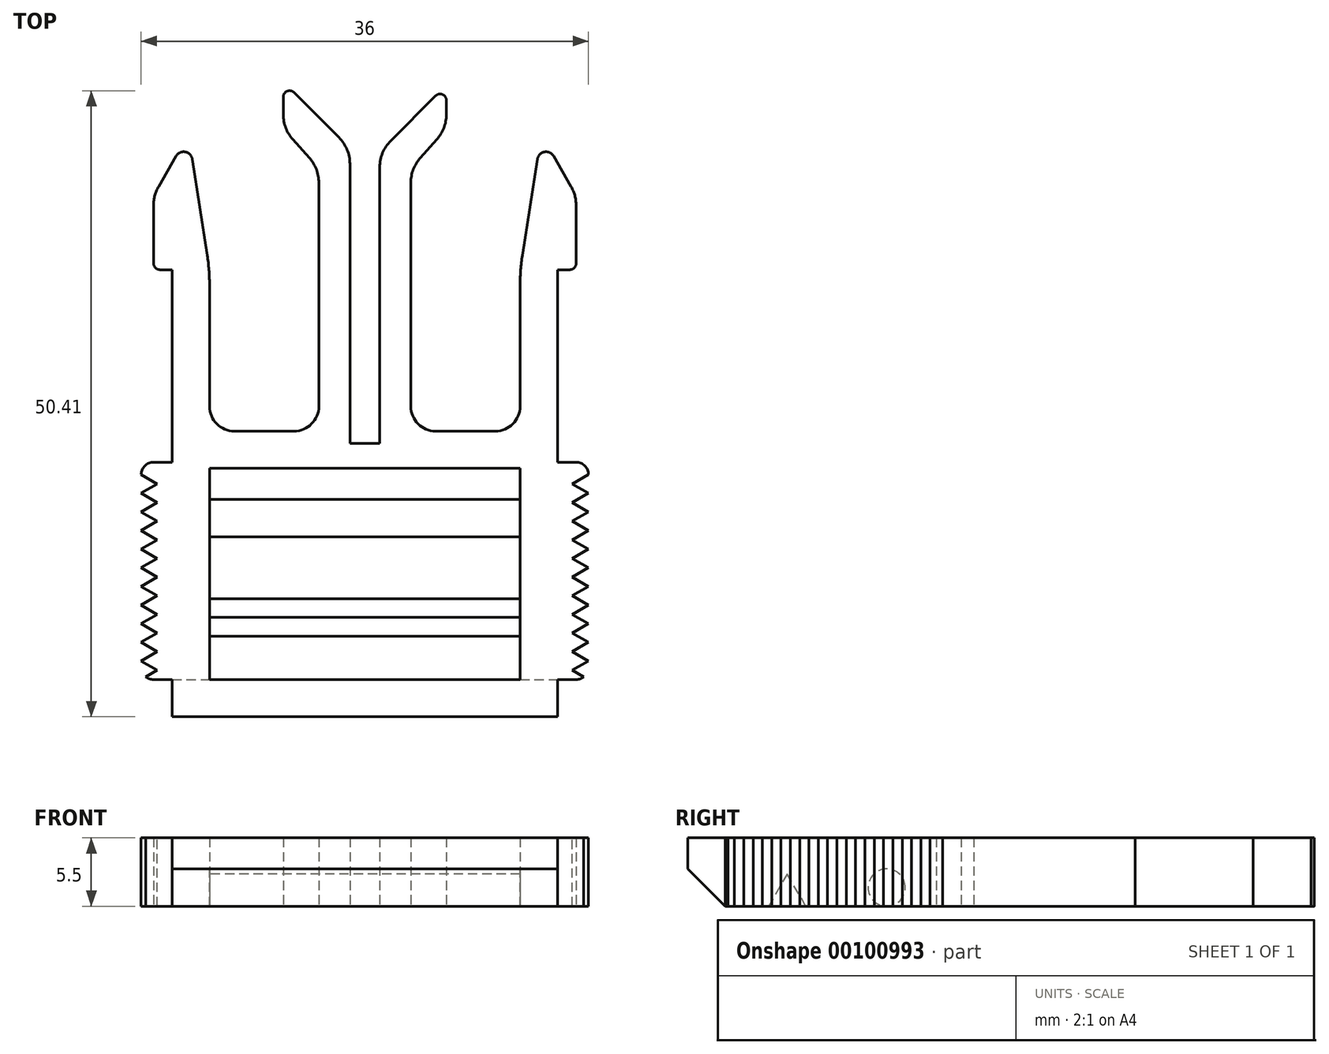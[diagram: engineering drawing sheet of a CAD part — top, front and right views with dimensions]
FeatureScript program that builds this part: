
annotation { "Feature Type Name" : "Feature", "Feature Type Description" : "" }
export const myFeature = defineFeature(function(context is Context, id is Id, definition is map)
    precondition{}
    {
        {
            var Q0;
            Q0=qCreatedBy(makeId("Top.planeOp"),FACE);
            var sketch = newSketch(context, id + "F0", { "sketchPlane" : qUnion([Q0])});
            skLineSegment(sketch, "E0.top", {"start": v(15.5, -24.35) * mm, "end": v(-15.5, -24.35) * mm});
            skPoint(sketch, "E0.middle", {"position": v(0, 0) * mm});
            skLineSegment(sketch, "E1.bottom", {"start": v(12.5, -4.35) * mm, "end": v(-12.5, -4.35) * mm});
            skLineSegment(sketch, "E1.top", {"start": v(12.5, -21.35) * mm, "end": v(-12.5, -21.35) * mm});
            skLineSegment(sketch, "E1.left", {"start": v(12.5, -4.35) * mm, "end": v(12.5, -21.35) * mm});
            skLineSegment(sketch, "E1.right", {"start": v(-12.5, -4.35) * mm, "end": v(-12.5, -21.35) * mm});
            skPoint(sketch, "E1.middle", {"position": v(0, -12.85) * mm});
            skLineSegment(sketch, "E2", {"start": v(15.18, 20.8) * mm, "end": v(16.6, 18.34) * mm});
            skLineSegment(sketch, "E3", {"start": v(17, 16.84) * mm, "end": v(17, 12.15) * mm});
            skLineSegment(sketch, "E4", {"start": v(16.5, 11.65) * mm, "end": v(15.5, 11.65) * mm});
            skLineSegment(sketch, "E5", {"start": v(0, -4.35) * mm, "end": v(0, 27.9) * mm, "construction": true});
            skLineSegment(sketch, "E6", {"start": v(-10.5, -1.35) * mm, "end": v(-5.7, -1.35) * mm});
            skLineSegment(sketch, "E7.trimOffspring", {"start": v(15.5, 11.65) * mm, "end": v(15.5, -24.35) * mm});
            skLineSegment(sketch, "E8", {"start": v(12.5, 10.49) * mm, "end": v(12.5, 0.65) * mm});
            skLineSegment(sketch, "E9.0", {"start": v(-3.7, 0.65) * mm, "end": v(-3.7, 18.65) * mm});
            skLineSegment(sketch, "E10.0", {"start": v(3.7, 0.65) * mm, "end": v(3.7, 18.65) * mm});
            skLineSegment(sketch, "E11", {"start": v(13.89, 20.55) * mm, "end": v(12.68, 12.8) * mm});
            skPoint(sketch, "E12.visualSharp", {"position": v(12.5, 11.65) * mm});
            skArc(sketch, "E12.filletArc", {"start": v(12.68, 12.8) * mm, "mid": v(12.54, 11.64) * mm, "end": v(12.5, 10.49) * mm});
            skLineSegment(sketch, "E13.trimOffspring", {"start": v(5.7, -1.35) * mm, "end": v(10.5, -1.35) * mm});
            skPoint(sketch, "E14.orphan", {"position": v(13.51, 18.14) * mm});
            skPoint(sketch, "E15.orphan", {"position": v(16.29, 18.88) * mm});
            skPoint(sketch, "E16.orphan", {"position": v(15.5, -1.35) * mm});
            skPoint(sketch, "E17.visualSharp", {"position": v(14.2, 22.51) * mm});
            skArc(sketch, "E17.filletArc", {"start": v(15.18, 20.8) * mm, "mid": v(14.45, 21.13) * mm, "end": v(13.89, 20.55) * mm});
            skArc(sketch, "E18.MirrorCS", {"start": v(-15.18, 20.8) * mm, "mid": v(-14.45, 21.13) * mm, "end": v(-13.89, 20.55) * mm});
            skLineSegment(sketch, "E19.MirrorCS", {"start": v(-15.18, 20.8) * mm, "end": v(-16.6, 18.34) * mm});
            skLineSegment(sketch, "E20.MirrorCS", {"start": v(-16.5, 11.65) * mm, "end": v(-15.5, 11.65) * mm});
            skPoint(sketch, "E21.MirrorP", {"position": v(-13.51, 18.14) * mm});
            skPoint(sketch, "E22.MirrorP", {"position": v(-12.5, 11.65) * mm});
            skArc(sketch, "E23.MirrorCS", {"start": v(-12.68, 12.8) * mm, "mid": v(-12.54, 11.64) * mm, "end": v(-12.5, 10.49) * mm});
            skPoint(sketch, "E24.MirrorP", {"position": v(-14.2, 22.51) * mm});
            skPoint(sketch, "E25.MirrorP", {"position": v(-16.29, 18.88) * mm});
            skLineSegment(sketch, "E26.MirrorCS", {"start": v(-17, 16.84) * mm, "end": v(-17, 12.15) * mm});
            skLineSegment(sketch, "E27.MirrorCS", {"start": v(-13.89, 20.55) * mm, "end": v(-12.68, 12.8) * mm});
            skLineSegment(sketch, "E28.MirrorCS", {"start": v(-15.5, 11.65) * mm, "end": v(-15.5, -24.35) * mm});
            skLineSegment(sketch, "E29.MirrorCS", {"start": v(-12.5, 10.49) * mm, "end": v(-12.5, 0.65) * mm});
            skLineSegment(sketch, "E30.0", {"start": v(1.2, -2.35) * mm, "end": v(1.2, 19.9) * mm});
            skLineSegment(sketch, "E31.0", {"start": v(-1.2, -2.35) * mm, "end": v(-1.2, 20.17) * mm});
            skLineSegment(sketch, "E32", {"start": v(5.7, 25.65) * mm, "end": v(2.08, 22.03) * mm});
            skLineSegment(sketch, "E33", {"start": v(-5.7, 25.92) * mm, "end": v(-2.08, 22.29) * mm});
            skPoint(sketch, "E34.visualSharp", {"position": v(17, 17.65) * mm});
            skArc(sketch, "E34.filletArc", {"start": v(17, 16.84) * mm, "mid": v(16.9, 17.62) * mm, "end": v(16.6, 18.34) * mm});
            skPoint(sketch, "E35.visualSharp", {"position": v(-17, 17.65) * mm});
            skArc(sketch, "E35.filletArc", {"start": v(-16.6, 18.34) * mm, "mid": v(-16.9, 17.62) * mm, "end": v(-17, 16.84) * mm});
            skLineSegment(sketch, "E36", {"start": v(-1.2, -2.35) * mm, "end": v(1.2, -2.35) * mm});
            skPoint(sketch, "E37.orphan", {"position": v(1.2, 0.65) * mm});
            skPoint(sketch, "E38.orphan", {"position": v(-1.2, 0.65) * mm});
            skLineSegment(sketch, "E39", {"start": v(4.46, 20.65) * mm, "end": v(5.8, 22.14) * mm});
            skLineSegment(sketch, "E40", {"start": v(6.56, 24.14) * mm, "end": v(6.56, 25.3) * mm});
            skLineSegment(sketch, "E41.MirrorCS", {"start": v(-4.46, 20.65) * mm, "end": v(-5.8, 22.14) * mm});
            skLineSegment(sketch, "E42.MirrorCS", {"start": v(-6.56, 24.14) * mm, "end": v(-6.56, 25.56) * mm});
            skPoint(sketch, "E43.newPointB", {"position": v(6.56, 27.77) * mm});
            skArc(sketch, "E43.filletArc", {"start": v(6.56, 25.3) * mm, "mid": v(6.25, 25.76) * mm, "end": v(5.7, 25.65) * mm});
            skPoint(sketch, "E44.newPointB", {"position": v(-6.56, 27.77) * mm});
            skArc(sketch, "E44.filletArc", {"start": v(-5.7, 25.92) * mm, "mid": v(-6.25, 26.03) * mm, "end": v(-6.56, 25.56) * mm});
            skPoint(sketch, "E45.orphan", {"position": v(3.7, 23.65) * mm});
            skPoint(sketch, "E46.orphan", {"position": v(-3.7, 23.91) * mm});
            skPoint(sketch, "E47.visualSharp", {"position": v(3.7, 19.8) * mm});
            skArc(sketch, "E47.filletArc", {"start": v(4.46, 20.65) * mm, "mid": v(3.9, 19.72) * mm, "end": v(3.7, 18.65) * mm});
            skPoint(sketch, "E48.visualSharp", {"position": v(1.2, 21.15) * mm});
            skArc(sketch, "E48.filletArc", {"start": v(2.08, 22.03) * mm, "mid": v(1.43, 21.05) * mm, "end": v(1.2, 19.9) * mm});
            skPoint(sketch, "E49.visualSharp", {"position": v(-1.2, 21.41) * mm});
            skArc(sketch, "E49.filletArc", {"start": v(-1.2, 20.17) * mm, "mid": v(-1.43, 21.32) * mm, "end": v(-2.08, 22.29) * mm});
            skPoint(sketch, "E50.visualSharp", {"position": v(-3.7, 19.8) * mm});
            skArc(sketch, "E50.filletArc", {"start": v(-3.7, 18.65) * mm, "mid": v(-3.9, 19.72) * mm, "end": v(-4.46, 20.65) * mm});
            skPoint(sketch, "E51.visualSharp", {"position": v(6.56, 23) * mm});
            skArc(sketch, "E51.filletArc", {"start": v(5.8, 22.14) * mm, "mid": v(6.36, 23.07) * mm, "end": v(6.56, 24.14) * mm});
            skPoint(sketch, "E52.visualSharp", {"position": v(-6.56, 23) * mm});
            skArc(sketch, "E52.filletArc", {"start": v(-6.56, 24.14) * mm, "mid": v(-6.36, 23.07) * mm, "end": v(-5.8, 22.14) * mm});
            skPoint(sketch, "E53.visualSharp", {"position": v(12.5, -1.35) * mm});
            skArc(sketch, "E53.filletArc", {"start": v(10.5, -1.35) * mm, "mid": v(11.91, -0.77) * mm, "end": v(12.5, 0.65) * mm});
            skPoint(sketch, "E54.visualSharp", {"position": v(-12.5, -1.35) * mm});
            skArc(sketch, "E54.filletArc", {"start": v(-12.5, 0.65) * mm, "mid": v(-11.91, -0.77) * mm, "end": v(-10.5, -1.35) * mm});
            skPoint(sketch, "E55.visualSharp", {"position": v(-3.7, -1.35) * mm});
            skArc(sketch, "E55.filletArc", {"start": v(-5.7, -1.35) * mm, "mid": v(-4.29, -0.77) * mm, "end": v(-3.7, 0.65) * mm});
            skPoint(sketch, "E56.visualSharp", {"position": v(3.7, -1.35) * mm});
            skArc(sketch, "E56.filletArc", {"start": v(3.7, 0.65) * mm, "mid": v(4.29, -0.77) * mm, "end": v(5.7, -1.35) * mm});
            skPoint(sketch, "E57.visualSharp", {"position": v(17, 11.65) * mm});
            skArc(sketch, "E57.filletArc", {"start": v(16.5, 11.65) * mm, "mid": v(16.85, 11.8) * mm, "end": v(17, 12.15) * mm});
            skPoint(sketch, "E58.visualSharp", {"position": v(-17, 11.65) * mm});
            skArc(sketch, "E58.filletArc", {"start": v(-17, 12.15) * mm, "mid": v(-16.85, 11.8) * mm, "end": v(-16.5, 11.65) * mm});
            skSolve(sketch);
        }
        {
            var Q0;
            Q0=makeQuery(id+"F0.imprint","IMPRINT",FACE,{"disambiguationData":[TD([[makeQuery(id+"F0.imprint","IMPRINT",EDGE,{"derivedFrom":sQuery(id+"F0.wireOp",EDGE,"E0.top")}),-1.0]])]});
            extrude(context, id + "F1", {"entities" : qUnion([Q0]), "depth" : 5.5 * mm});
        }
        {
            var Q0;
            Q0=makeQuery(id+"F1.opExtrude","SWEPT_FACE",FACE,{"disambiguationData":[OSD([sQuery(id+"F0.wireOp",EDGE,"E1.right")])]});
            var sketch = newSketch(context, id + "F2", { "sketchPlane" : qUnion([Q0])});
            skLineSegment(sketch, "E59", {"start": v(-16.35, 2.6) * mm, "end": v(-17.85, 0) * mm});
            skLineSegment(sketch, "E60", {"start": v(-17.85, 0) * mm, "end": v(-14.85, 0) * mm});
            skLineSegment(sketch, "E61", {"start": v(-14.85, 0) * mm, "end": v(-16.35, 2.6) * mm});
            skCircle(sketch, "E62", {"center": v(-8.35, 1.5) * mm, "radius": 1.5 * mm});
            skPoint(sketch, "E62.centerSnap0", {"position": v(-4.35, 2.75) * mm});
            skSolve(sketch);
        }
        {
            var Q0;
            Q0=makeQuery(id+"F2.imprint","IMPRINT",FACE,{"disambiguationData":[TD([[makeQuery(id+"F2.imprint","IMPRINT",EDGE,{"derivedFrom":sQuery(id+"F2.wireOp",EDGE,"E59")}),1.0]])]});
            var Q1;
            Q1=makeQuery(id+"F2.imprint","IMPRINT",FACE,{"disambiguationData":[TD([[makeQuery(id+"F2.imprint","IMPRINT",EDGE,{"derivedFrom":sQuery(id+"F2.wireOp",EDGE,"E62")}),1.0]])]});
            extrude(context, id + "F3", {"entities" : qUnion([Q0, Q1]), "operationType" : NewBodyOperationType.ADD, "depth" : 25 * mm});
        }
        {
            var Q0;
            Q0=makeQuery(id+"F1.opExtrude","SWEPT_FACE",FACE,{"disambiguationData":[OSD([sQuery(id+"F0.wireOp",EDGE,"E7.trimOffspring")])]});
            var sketch = newSketch(context, id + "F4", { "sketchPlane" : qUnion([Q0])});
            skLineSegment(sketch, "E63", {"start": v(-21.35, 0) * mm, "end": v(-24.35, 3) * mm});
            skSolve(sketch);
        }
        {
            var Q0;
            {var subQ0=sQuery(id+"F4.wireOp",EDGE,"E63");Q0=makeQuery(id+"F4.imprint","IMPRINT",FACE,{"disambiguationData":[TD([[makeQuery(id+"F4.imprint","IMPRINT",EDGE,{"derivedFrom":subQ0}),1.0]])]});}
            var Q1;
            Q1=makeQuery(id+"F1.opExtrude","SWEPT_FACE",FACE,{"disambiguationData":[OSD([sQuery(id+"F0.wireOp",EDGE,"E1.right")])]});
            var Q2;
            Q2=makeQuery(id+"F1.opExtrude","SWEPT_FACE",FACE,{"disambiguationData":[OSD([sQuery(id+"F0.wireOp",EDGE,"E1.left")])]});
            extrude(context, id + "F5", {"entities" : qUnion([Q0]), "operationType" : NewBodyOperationType.REMOVE, "endBound" : BoundingType.THROUGH_ALL, "oppositeDirection" : true, "endBoundEntityFace" : qUnion([Q1]), "depth" : 25 * mm});
        }
        {
            var Q0;
            Q0=makeQuery(id+"F1.opExtrude","CAP_FACE",FACE,{"disambiguationData":[OSD([sQuery(id+"F0.wireOp",EDGE,"E0.top"),sQuery(id+"F0.wireOp",EDGE,"E1.bottom"),sQuery(id+"F0.wireOp",EDGE,"E1.top"),sQuery(id+"F0.wireOp",EDGE,"E1.left"),sQuery(id+"F0.wireOp",EDGE,"E1.right"),sQuery(id+"F0.wireOp",EDGE,"E2"),sQuery(id+"F0.wireOp",EDGE,"E3"),sQuery(id+"F0.wireOp",EDGE,"E4"),sQuery(id+"F0.wireOp",EDGE,"E6"),sQuery(id+"F0.wireOp",EDGE,"E7.trimOffspring"),sQuery(id+"F0.wireOp",EDGE,"E8"),sQuery(id+"F0.wireOp",EDGE,"E9.0"),sQuery(id+"F0.wireOp",EDGE,"E10.0"),sQuery(id+"F0.wireOp",EDGE,"E11"),sQuery(id+"F0.wireOp",EDGE,"E12.filletArc"),sQuery(id+"F0.wireOp",EDGE,"E13.trimOffspring"),sQuery(id+"F0.wireOp",EDGE,"E17.filletArc"),sQuery(id+"F0.wireOp",EDGE,"E18.MirrorCS"),sQuery(id+"F0.wireOp",EDGE,"E19.MirrorCS"),sQuery(id+"F0.wireOp",EDGE,"E20.MirrorCS"),sQuery(id+"F0.wireOp",EDGE,"E23.MirrorCS"),sQuery(id+"F0.wireOp",EDGE,"E26.MirrorCS"),sQuery(id+"F0.wireOp",EDGE,"E27.MirrorCS"),sQuery(id+"F0.wireOp",EDGE,"E28.MirrorCS"),sQuery(id+"F0.wireOp",EDGE,"E29.MirrorCS"),sQuery(id+"F0.wireOp",EDGE,"E30.0"),sQuery(id+"F0.wireOp",EDGE,"E31.0"),sQuery(id+"F0.wireOp",EDGE,"UTjdTIHE-D38J-cQlS-tRNC-KbjzHWpZoidh"),sQuery(id+"F0.wireOp",EDGE,"E32"),sQuery(id+"F0.wireOp",EDGE,"E33"),sQuery(id+"F0.wireOp",EDGE,"E34.filletArc"),sQuery(id+"F0.wireOp",EDGE,"E35.filletArc")])],"isStart":false});
            var sketch = newSketch(context, id + "F6", { "sketchPlane" : qUnion([Q0])});
            skLineSegment(sketch, "E64", {"start": v(15.5, -3.85) * mm, "end": v(17, -3.85) * mm});
            skLineSegment(sketch, "E65", {"start": v(18, -4.85) * mm, "end": v(18, -20.35) * mm});
            skLineSegment(sketch, "E66", {"start": v(17, -21.35) * mm, "end": v(15.5, -21.35) * mm});
            skPoint(sketch, "E67.visualSharp", {"position": v(18, -3.85) * mm});
            skArc(sketch, "E67.filletArc", {"start": v(18, -4.85) * mm, "mid": v(17.7, -4.15) * mm, "end": v(17, -3.85) * mm});
            skPoint(sketch, "E68.visualSharp", {"position": v(18, -21.35) * mm});
            skArc(sketch, "E68.filletArc", {"start": v(17, -21.35) * mm, "mid": v(17.7, -21.06) * mm, "end": v(18, -20.35) * mm});
            skLineSegment(sketch, "E69", {"start": v(15.5, -3.85) * mm, "end": v(15.5, -21.35) * mm});
            skSolve(sketch);
        }
        {
            var Q0;
            Q0=makeQuery(id+"F6.imprint","IMPRINT",FACE,{"disambiguationData":[TD([[makeQuery(id+"F6.imprint","IMPRINT",EDGE,{"derivedFrom":sQuery(id+"F6.wireOp",EDGE,"E64")}),-1.0]])]});
            var Q1;
            Q1=makeQuery(id+"F1.opExtrude","CAP_FACE",FACE,{"disambiguationData":[OSD([sQuery(id+"F0.wireOp",EDGE,"E0.top"),sQuery(id+"F0.wireOp",EDGE,"E1.bottom"),sQuery(id+"F0.wireOp",EDGE,"E1.top"),sQuery(id+"F0.wireOp",EDGE,"E1.left"),sQuery(id+"F0.wireOp",EDGE,"E1.right"),sQuery(id+"F0.wireOp",EDGE,"E2"),sQuery(id+"F0.wireOp",EDGE,"E3"),sQuery(id+"F0.wireOp",EDGE,"E4"),sQuery(id+"F0.wireOp",EDGE,"E6"),sQuery(id+"F0.wireOp",EDGE,"E7.trimOffspring"),sQuery(id+"F0.wireOp",EDGE,"E8"),sQuery(id+"F0.wireOp",EDGE,"E9.0"),sQuery(id+"F0.wireOp",EDGE,"E10.0"),sQuery(id+"F0.wireOp",EDGE,"E11"),sQuery(id+"F0.wireOp",EDGE,"E12.filletArc"),sQuery(id+"F0.wireOp",EDGE,"E13.trimOffspring"),sQuery(id+"F0.wireOp",EDGE,"E17.filletArc"),sQuery(id+"F0.wireOp",EDGE,"E18.MirrorCS"),sQuery(id+"F0.wireOp",EDGE,"E19.MirrorCS"),sQuery(id+"F0.wireOp",EDGE,"E20.MirrorCS"),sQuery(id+"F0.wireOp",EDGE,"E23.MirrorCS"),sQuery(id+"F0.wireOp",EDGE,"E26.MirrorCS"),sQuery(id+"F0.wireOp",EDGE,"E27.MirrorCS"),sQuery(id+"F0.wireOp",EDGE,"E28.MirrorCS"),sQuery(id+"F0.wireOp",EDGE,"E29.MirrorCS"),sQuery(id+"F0.wireOp",EDGE,"E30.0"),sQuery(id+"F0.wireOp",EDGE,"E31.0"),sQuery(id+"F0.wireOp",EDGE,"UTjdTIHE-D38J-cQlS-tRNC-KbjzHWpZoidh"),sQuery(id+"F0.wireOp",EDGE,"E32"),sQuery(id+"F0.wireOp",EDGE,"E33"),sQuery(id+"F0.wireOp",EDGE,"E34.filletArc"),sQuery(id+"F0.wireOp",EDGE,"E35.filletArc")])],"isStart":true});
            extrude(context, id + "F7", {"entities" : qUnion([Q0]), "endBound" : BoundingType.UP_TO_SURFACE, "oppositeDirection" : true, "endBoundEntityFace" : qUnion([Q1]), "depth" : 25 * mm});
        }
        {
            var Q0;
            Q0=makeQuery(id+"F7.opExtrude","CAP_FACE",FACE,{"disambiguationData":[OSD([sQuery(id+"F6.wireOp",EDGE,"E64"),sQuery(id+"F6.wireOp",EDGE,"E65"),sQuery(id+"F6.wireOp",EDGE,"E66"),sQuery(id+"F6.wireOp",EDGE,"E67.filletArc"),sQuery(id+"F6.wireOp",EDGE,"E68.filletArc"),sQuery(id+"F6.wireOp",EDGE,"E69")])],"isStart":true});
            var sketch = newSketch(context, id + "F8", { "sketchPlane" : qUnion([Q0])});
            skLineSegment(sketch, "E70", {"start": v(18, -4.85) * mm, "end": v(16.7, -5.6) * mm});
            skLineSegment(sketch, "E71", {"start": v(16.7, -5.6) * mm, "end": v(18, -6.35) * mm});
            skLineSegment(sketch, "E72", {"start": v(18, -6.35) * mm, "end": v(18, -4.85) * mm});
            skLineSegment(sketch, "E73.0.1.0", {"start": v(18, -7.85) * mm, "end": v(18, -6.35) * mm});
            skLineSegment(sketch, "E73.0.1.1", {"start": v(16.7, -7.1) * mm, "end": v(18, -7.85) * mm});
            skLineSegment(sketch, "E73.0.1.2", {"start": v(18, -6.35) * mm, "end": v(16.7, -7.1) * mm});
            skLineSegment(sketch, "E73.0.2.0", {"start": v(18, -9.35) * mm, "end": v(18, -7.85) * mm});
            skLineSegment(sketch, "E73.0.2.1", {"start": v(16.7, -8.6) * mm, "end": v(18, -9.35) * mm});
            skLineSegment(sketch, "E73.0.2.2", {"start": v(18, -7.85) * mm, "end": v(16.7, -8.6) * mm});
            skLineSegment(sketch, "E73.0.3.0", {"start": v(18, -10.85) * mm, "end": v(18, -9.35) * mm});
            skLineSegment(sketch, "E73.0.3.1", {"start": v(16.7, -10.1) * mm, "end": v(18, -10.85) * mm});
            skLineSegment(sketch, "E73.0.3.2", {"start": v(18, -9.35) * mm, "end": v(16.7, -10.1) * mm});
            skLineSegment(sketch, "E73.0.4.0", {"start": v(18, -12.35) * mm, "end": v(18, -10.85) * mm});
            skLineSegment(sketch, "E73.0.4.1", {"start": v(16.7, -11.6) * mm, "end": v(18, -12.35) * mm});
            skLineSegment(sketch, "E73.0.4.2", {"start": v(18, -10.85) * mm, "end": v(16.7, -11.6) * mm});
            skLineSegment(sketch, "E73.0.5.0", {"start": v(18, -13.85) * mm, "end": v(18, -12.35) * mm});
            skLineSegment(sketch, "E73.0.5.1", {"start": v(16.7, -13.1) * mm, "end": v(18, -13.85) * mm});
            skLineSegment(sketch, "E73.0.5.2", {"start": v(18, -12.35) * mm, "end": v(16.7, -13.1) * mm});
            skLineSegment(sketch, "E73.0.6.0", {"start": v(18, -15.35) * mm, "end": v(18, -13.85) * mm});
            skLineSegment(sketch, "E73.0.6.1", {"start": v(16.7, -14.6) * mm, "end": v(18, -15.35) * mm});
            skLineSegment(sketch, "E73.0.6.2", {"start": v(18, -13.85) * mm, "end": v(16.7, -14.6) * mm});
            skLineSegment(sketch, "E73.0.7.0", {"start": v(18, -16.85) * mm, "end": v(18, -15.35) * mm});
            skLineSegment(sketch, "E73.0.7.1", {"start": v(16.7, -16.1) * mm, "end": v(18, -16.85) * mm});
            skLineSegment(sketch, "E73.0.7.2", {"start": v(18, -15.35) * mm, "end": v(16.7, -16.1) * mm});
            skLineSegment(sketch, "E73.0.8.0", {"start": v(18, -18.35) * mm, "end": v(18, -16.85) * mm});
            skLineSegment(sketch, "E73.0.8.1", {"start": v(16.7, -17.6) * mm, "end": v(18, -18.35) * mm});
            skLineSegment(sketch, "E73.0.8.2", {"start": v(18, -16.85) * mm, "end": v(16.7, -17.6) * mm});
            skLineSegment(sketch, "E73.0.9.0", {"start": v(18, -19.85) * mm, "end": v(18, -18.35) * mm});
            skLineSegment(sketch, "E73.0.9.1", {"start": v(16.7, -19.1) * mm, "end": v(18, -19.85) * mm});
            skLineSegment(sketch, "E73.0.9.2", {"start": v(18, -18.35) * mm, "end": v(16.7, -19.1) * mm});
            skLineSegment(sketch, "E73.0.10.0", {"start": v(18, -21.35) * mm, "end": v(18, -19.85) * mm});
            skLineSegment(sketch, "E73.0.10.1", {"start": v(16.7, -20.6) * mm, "end": v(18, -21.35) * mm});
            skLineSegment(sketch, "E73.0.10.2", {"start": v(18, -19.85) * mm, "end": v(16.7, -20.6) * mm});
            skLineSegment(sketch, "E73.direction1", {"start": v(18, -6.35) * mm, "end": v(36.9, -6.35) * mm, "construction": true});
            skLineSegment(sketch, "E73.direction2", {"start": v(18, -6.35) * mm, "end": v(18, -7.85) * mm, "construction": true});
            skLineSegment(sketch, "E74", {"start": v(0, 0) * mm, "end": v(0, -26.7) * mm, "construction": true});
            skSolve(sketch);
        }
        {
            var Q0;
            Q0 = qSketchRegion(id + "F8", true);
            extrude(context, id + "F9", {"entities" : qUnion([Q0]), "operationType" : NewBodyOperationType.REMOVE, "endBound" : BoundingType.THROUGH_ALL, "oppositeDirection" : true, "depth" : 25 * mm});
        }
        {
            var Q0;
            Q0=makeQuery(id+"F1.opExtrude","SWEPT_FACE",FACE,{"disambiguationData":[OSD([sQuery(id+"F0.wireOp",EDGE,"E7.trimOffspring")])]});
            var Q1;
            Q1=makeQuery(id+"F1.opExtrude","SWEPT_FACE",FACE,{"disambiguationData":[OSD([sQuery(id+"F0.wireOp",EDGE,"E28.MirrorCS")])]});
            cPlane(context, id + "F10", {"entities" : qUnion([Q0, Q1]), "cplaneType" : CPlaneType.MID_PLANE, "offset" : 150 * mm, "width" : 150 * mm, "height" : 150 * mm});
        }
        {
            var Q0;
            Q0=makeQuery(id+"F7.opExtrude","SWEPT_BODY",BODY,{"disambiguationData":[OSD([sQuery(id+"F6.wireOp",EDGE,"E64"),sQuery(id+"F6.wireOp",EDGE,"E65"),sQuery(id+"F6.wireOp",EDGE,"E66"),sQuery(id+"F6.wireOp",EDGE,"E67.filletArc"),sQuery(id+"F6.wireOp",EDGE,"E68.filletArc"),sQuery(id+"F6.wireOp",EDGE,"E69")])]});
            var Q1;
            Q1=qCreatedBy(id+"F10.planeOp",FACE);
            mirror(context, id + "F11", {"operationType" : NewBodyOperationType.ADD, "entities" : qUnion([Q0]), "mirrorPlane" : qUnion([Q1])});
        }
    });
